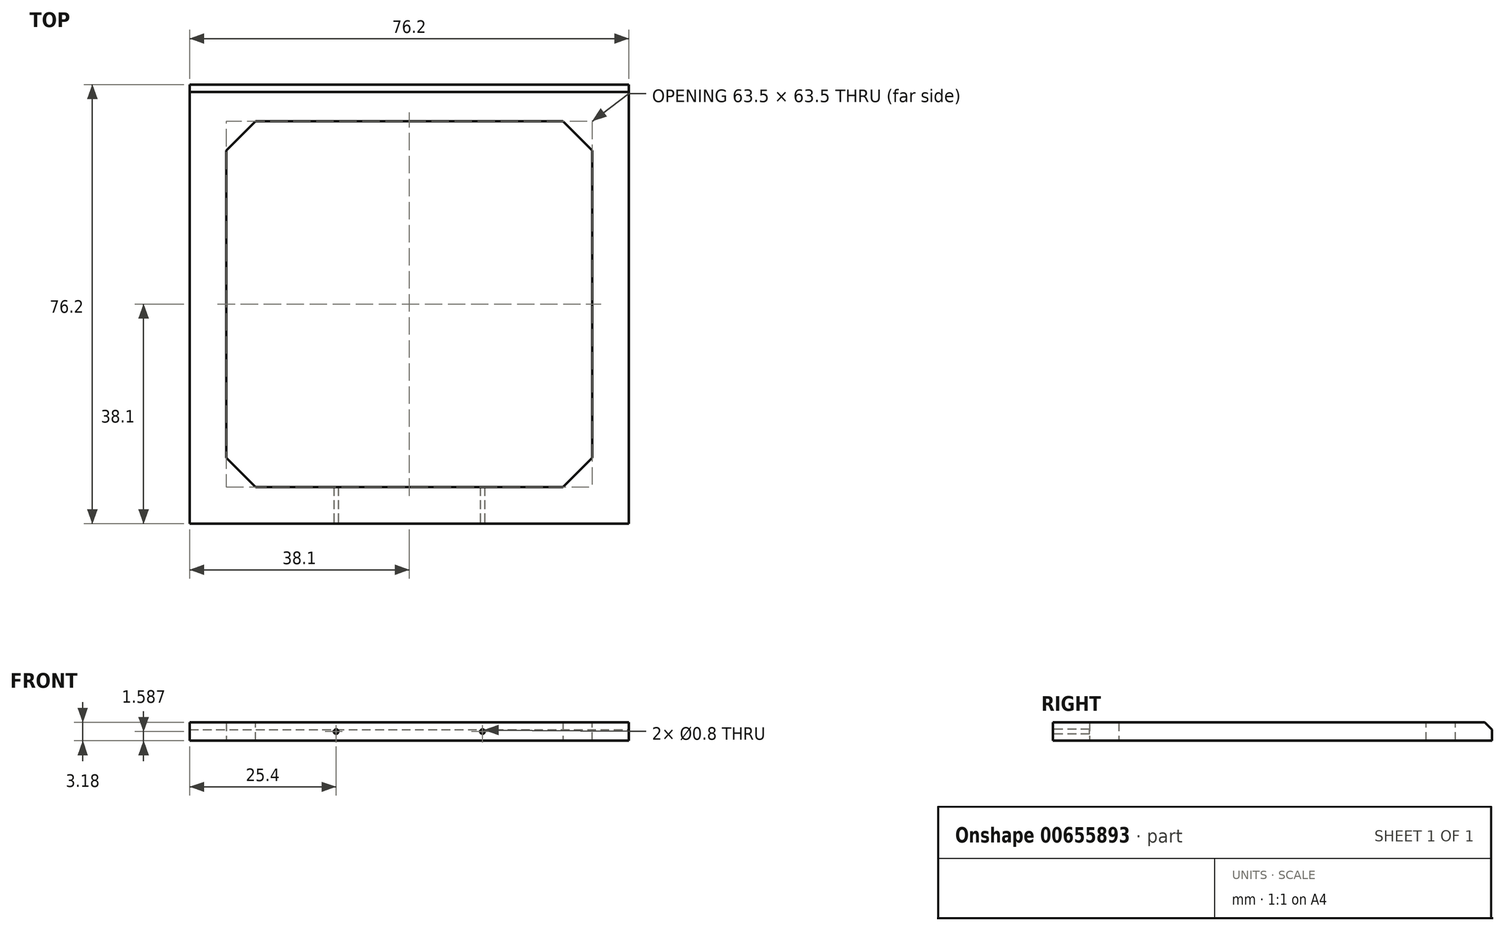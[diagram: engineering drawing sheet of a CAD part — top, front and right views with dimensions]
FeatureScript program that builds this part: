
annotation { "Feature Type Name" : "Feature", "Feature Type Description" : "" }
export const myFeature = defineFeature(function(context is Context, id is Id, definition is map)
    precondition{}
    {
        {
            var Q0;
            Q0=qCreatedBy(makeId("Top.planeOp"),FACE);
            var sketch = newSketch(context, id + "F0", { "sketchPlane" : qUnion([Q0])});
            skLineSegment(sketch, "E0.bottom", {"start": v(-38.1, -38.1) * mm, "end": v(38.1, -38.1) * mm});
            skLineSegment(sketch, "E0.top", {"start": v(-38.1, 38.1) * mm, "end": v(38.1, 38.1) * mm});
            skLineSegment(sketch, "E0.left", {"start": v(-38.1, -38.1) * mm, "end": v(-38.1, 38.1) * mm});
            skLineSegment(sketch, "E0.right", {"start": v(38.1, -38.1) * mm, "end": v(38.1, 38.1) * mm});
            skPoint(sketch, "E0.middle", {"position": v(0, 0) * mm});
            skLineSegment(sketch, "E1.bottom", {"start": v(-31.75, -31.75) * mm, "end": v(31.75, -31.75) * mm});
            skLineSegment(sketch, "E1.top", {"start": v(-31.75, 31.75) * mm, "end": v(31.75, 31.75) * mm});
            skLineSegment(sketch, "E1.left", {"start": v(-31.75, -31.75) * mm, "end": v(-31.75, 31.75) * mm});
            skLineSegment(sketch, "E1.right", {"start": v(31.75, -31.75) * mm, "end": v(31.75, 31.75) * mm});
            skSolve(sketch);
        }
        {
            var Q0;
            Q0=makeQuery(id+"F0.imprint","IMPRINT",FACE,{"disambiguationData":[TD([[makeQuery(id+"F0.imprint","IMPRINT",EDGE,{"derivedFrom":sQuery(id+"F0.wireOp",EDGE,"E0.bottom")}),1.0]])]});
            extrude(context, id + "F1", {"entities" : qUnion([Q0]), "depth" : 3.17 * mm, "offsetDistance" : 25.4 * mm});
        }
        {
            var Q0;
            Q0=makeQuery(id+"F1.opExtrude","SWEPT_EDGE",EDGE,{"disambiguationData":[OSD([sQuery(id+"F0.wireOp",EDGE,"E1.top"),sQuery(id+"F0.wireOp",EDGE,"E1.left")])]});
            chamfer(context, id + "F2", {"entities" : qUnion([Q0]), "width" : 5.08 * mm, "tangentPropagation" : true});
        }
        {
            var Q0;
            Q0=makeQuery(id+"F1.opExtrude","SWEPT_EDGE",EDGE,{"disambiguationData":[OSD([sQuery(id+"F0.wireOp",EDGE,"E1.top"),sQuery(id+"F0.wireOp",EDGE,"E1.right")])]});
            chamfer(context, id + "F3", {"entities" : qUnion([Q0]), "width" : 5.08 * mm, "tangentPropagation" : true});
        }
        {
            var Q0;
            Q0=makeQuery(id+"F1.opExtrude","SWEPT_EDGE",EDGE,{"disambiguationData":[OSD([sQuery(id+"F0.wireOp",EDGE,"E1.bottom"),sQuery(id+"F0.wireOp",EDGE,"E1.left")])]});
            chamfer(context, id + "F4", {"entities" : qUnion([Q0]), "width" : 5.08 * mm, "tangentPropagation" : true});
        }
        {
            var Q0;
            Q0=makeQuery(id+"F1.opExtrude","SWEPT_EDGE",EDGE,{"disambiguationData":[OSD([sQuery(id+"F0.wireOp",EDGE,"E1.bottom"),sQuery(id+"F0.wireOp",EDGE,"E1.right")])]});
            chamfer(context, id + "F5", {"entities" : qUnion([Q0]), "width" : 5.08 * mm, "tangentPropagation" : true});
        }
        {
            var Q0;
            Q0=makeQuery(id+"F1.opExtrude","CAP_EDGE",EDGE,{"disambiguationData":[OSD([sQuery(id+"F0.wireOp",EDGE,"E0.top")])],"isStart":false});
            chamfer(context, id + "F6", {"entities" : qUnion([Q0]), "width" : 1.27 * mm, "tangentPropagation" : true});
        }
        {
            var Q0;
            Q0=makeQuery(id+"F1.opExtrude","SWEPT_FACE",FACE,{"disambiguationData":[OSD([sQuery(id+"F0.wireOp",EDGE,"E0.bottom")])]});
            var sketch = newSketch(context, id + "F7", { "sketchPlane" : qUnion([Q0])});
            skCircle(sketch, "E2", {"center": v(-12.7, 1.59) * mm, "radius": 0.4 * mm});
            skCircle(sketch, "E3", {"center": v(12.7, 1.59) * mm, "radius": 0.4 * mm});
            skSolve(sketch);
        }
        {
            var Q0;
            Q0 = qSketchRegion(id + "F7", true);
            extrude(context, id + "F8", {"entities" : qUnion([Q0]), "operationType" : NewBodyOperationType.REMOVE, "oppositeDirection" : true, "depth" : 6.35 * mm, "offsetDistance" : 25.4 * mm});
        }
    });
